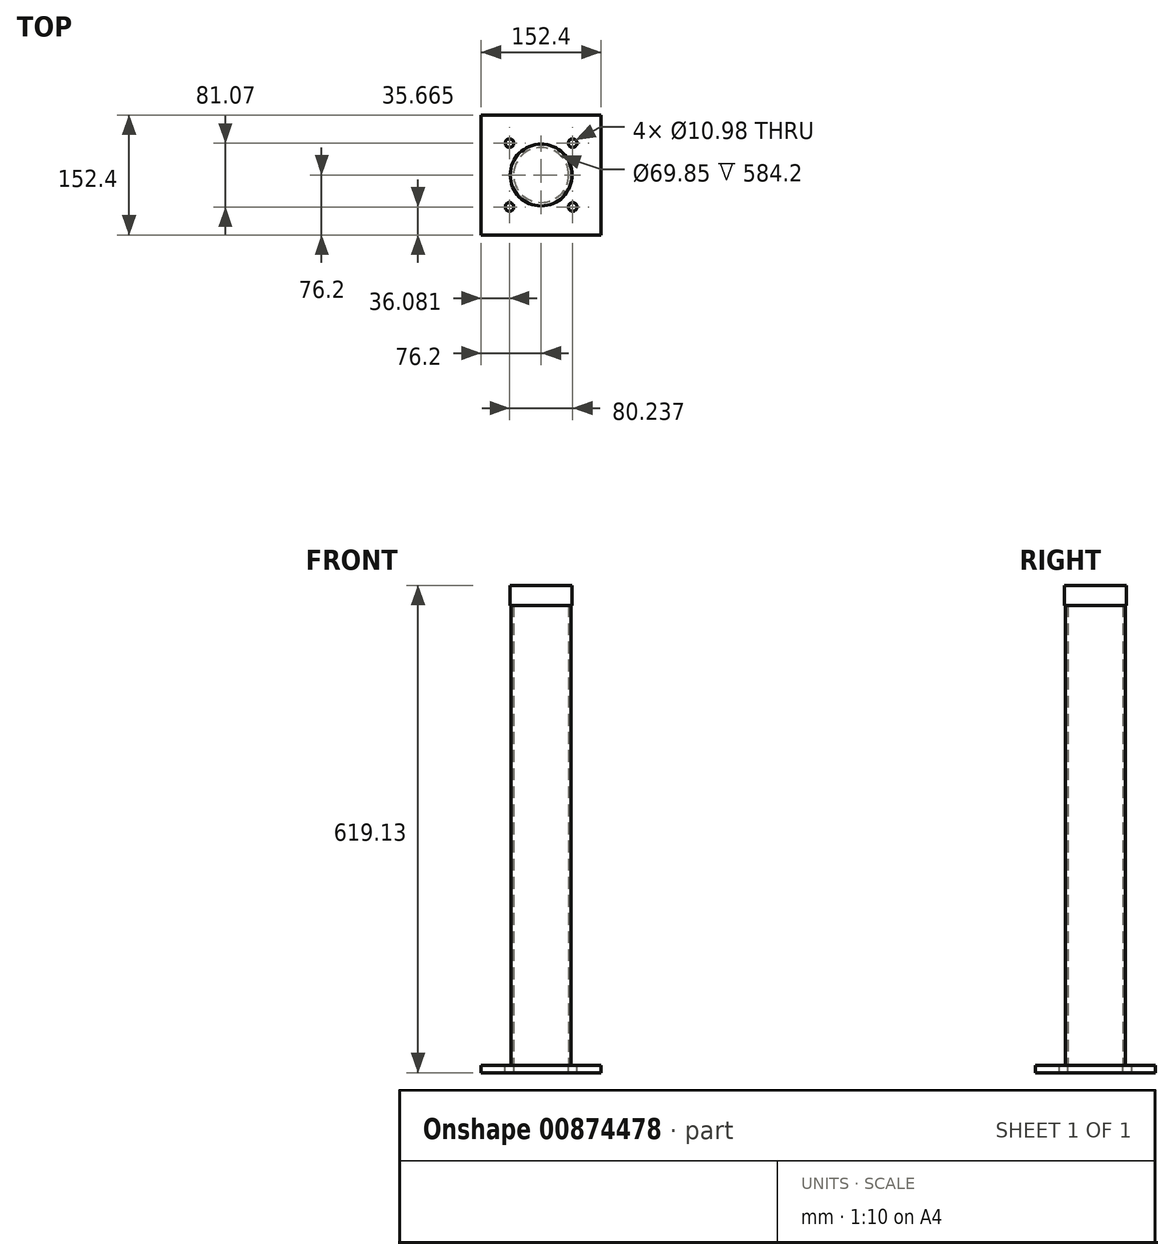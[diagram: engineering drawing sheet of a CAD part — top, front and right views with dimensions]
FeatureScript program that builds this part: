
annotation { "Feature Type Name" : "Feature", "Feature Type Description" : "" }
export const myFeature = defineFeature(function(context is Context, id is Id, definition is map)
    precondition{}
    {
        {
            var Q0;
            Q0=qCreatedBy(makeId("Top.planeOp"),FACE);
            var sketch = newSketch(context, id + "F0", { "sketchPlane" : qUnion([Q0])});
            skCircle(sketch, "E0", {"center": v(0, 0) * mm, "radius": 38.1 * mm});
            skCircle(sketch, "E1", {"center": v(0, 0) * mm, "radius": 34.93 * mm});
            skSolve(sketch);
        }
        {
            var Q0;
            Q0=makeQuery(id+"F0.imprint","IMPRINT",FACE,{"disambiguationData":[TD([[makeQuery(id+"F0.imprint","IMPRINT",EDGE,{"derivedFrom":sQuery(id+"F0.wireOp",EDGE,"E0")}),1.0]])]});
            extrude(context, id + "F1", {"entities" : qUnion([Q0]), "depth" : 609.6 * mm, "offsetDistance" : 25.4 * mm});
        }
        {
            var Q0;
            Q0=qCreatedBy(makeId("Top.planeOp"),FACE);
            var sketch = newSketch(context, id + "F2", { "sketchPlane" : qUnion([Q0])});
            skLineSegment(sketch, "E2.bottom", {"start": v(-76.2, 76.2) * mm, "end": v(76.2, 76.2) * mm});
            skLineSegment(sketch, "E2.top", {"start": v(-76.2, -76.2) * mm, "end": v(76.2, -76.2) * mm});
            skLineSegment(sketch, "E2.left", {"start": v(-76.2, 76.2) * mm, "end": v(-76.2, -76.2) * mm});
            skLineSegment(sketch, "E2.right", {"start": v(76.2, 76.2) * mm, "end": v(76.2, -76.2) * mm});
            skPoint(sketch, "E2.middle", {"position": v(0, 0) * mm});
            skCircle(sketch, "E3", {"center": v(40.12, 40.53) * mm, "radius": 5.49 * mm});
            skCircle(sketch, "E4.MirrorC", {"center": v(-40.12, 40.53) * mm, "radius": 5.49 * mm});
            skCircle(sketch, "E5.MirrorC", {"center": v(-40.12, -40.53) * mm, "radius": 5.49 * mm});
            skCircle(sketch, "E6.MirrorC", {"center": v(40.12, -40.53) * mm, "radius": 5.49 * mm});
            skSolve(sketch);
        }
        {
            var Q0;
            Q0=makeQuery(id+"F2.imprint","IMPRINT",FACE,{"disambiguationData":[TD([[makeQuery(id+"F2.imprint","IMPRINT",EDGE,{"derivedFrom":sQuery(id+"F2.wireOp",EDGE,"E2.bottom")}),-1.0]])]});
            extrude(context, id + "F3", {"entities" : qUnion([Q0]), "operationType" : NewBodyOperationType.ADD, "oppositeDirection" : true, "depth" : 9.52 * mm, "offsetDistance" : 25.4 * mm});
        }
        {
            var Q0;
            Q0=makeQuery(id+"F1.opExtrude","CAP_FACE",FACE,{"disambiguationData":[OSD([sQuery(id+"F0.wireOp",EDGE,"E0"),sQuery(id+"F0.wireOp",EDGE,"E1")])],"isStart":false});
            var sketch = newSketch(context, id + "F4", { "sketchPlane" : qUnion([Q0])});
            skCircle(sketch, "E7", {"center": v(0, 0) * mm, "radius": 39.29 * mm});
            skSolve(sketch);
        }
        {
            var Q0;
            Q0 = qSketchRegion(id + "F4", true);
            extrude(context, id + "F5", {"entities" : qUnion([Q0]), "operationType" : NewBodyOperationType.ADD, "oppositeDirection" : true, "depth" : 25.4 * mm, "offsetDistance" : 25.4 * mm});
        }
    });
